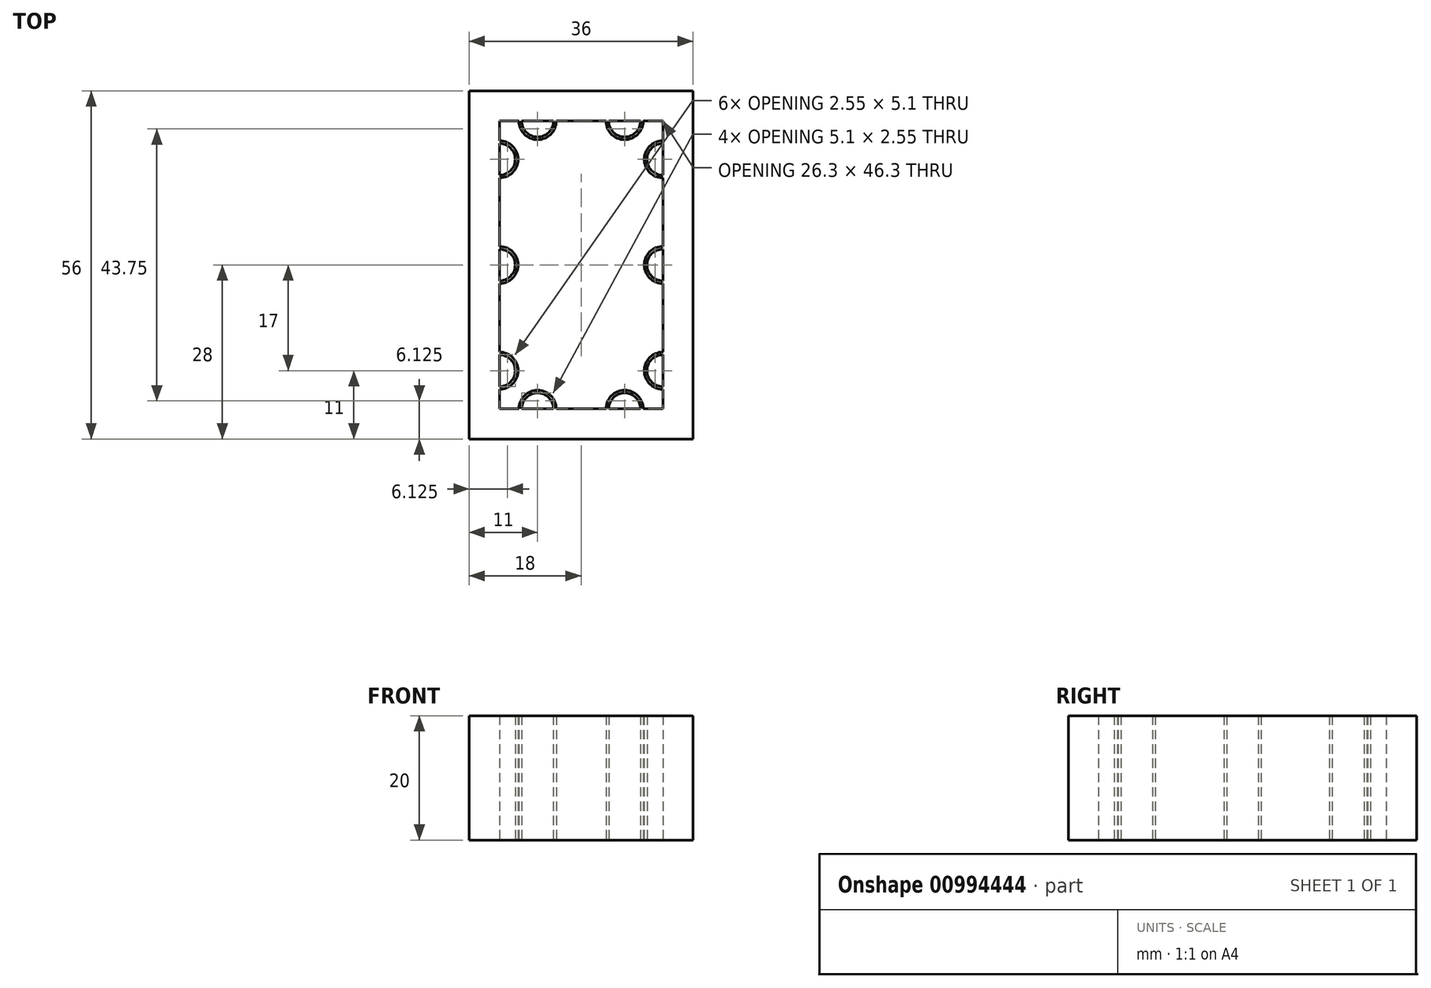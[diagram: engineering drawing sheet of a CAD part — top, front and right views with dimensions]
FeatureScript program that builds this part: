
annotation { "Feature Type Name" : "Feature", "Feature Type Description" : "" }
export const myFeature = defineFeature(function(context is Context, id is Id, definition is map)
    precondition{}
    {
        {
            var Q0;
            Q0=qCreatedBy(makeId("Top.planeOp"),FACE);
            var sketch = newSketch(context, id + "F0", { "sketchPlane" : qUnion([Q0])});
            skLineSegment(sketch, "E0.bottom", {"start": v(0, 0) * mm, "end": v(20, 0) * mm, "construction": true});
            skLineSegment(sketch, "E0.top", {"start": v(0, 40) * mm, "end": v(20, 40) * mm, "construction": true});
            skLineSegment(sketch, "E0.left", {"start": v(0, 0) * mm, "end": v(0, 40) * mm, "construction": true});
            skLineSegment(sketch, "E0.right", {"start": v(20, 0) * mm, "end": v(20, 40) * mm, "construction": true});
            skLineSegment(sketch, "E1", {"start": v(6, 40) * mm, "end": v(6, 34) * mm, "construction": true});
            skLineSegment(sketch, "E2", {"start": v(14, 40) * mm, "end": v(14, 34) * mm, "construction": true});
            skLineSegment(sketch, "E3", {"start": v(1, 27) * mm, "end": v(1, 13) * mm, "construction": true});
            skLineSegment(sketch, "E4", {"start": v(19, 27) * mm, "end": v(19, 13) * mm, "construction": true});
            skLineSegment(sketch, "E5", {"start": v(14, 6) * mm, "end": v(14, 0) * mm, "construction": true});
            skLineSegment(sketch, "E6", {"start": v(6, 6) * mm, "end": v(6, 0) * mm, "construction": true});
            skPoint(sketch, "E7.centerSnap0", {"position": v(6, 37) * mm});
            skPoint(sketch, "E8.centerSnap0", {"position": v(14, 37) * mm});
            skPoint(sketch, "E9.centerSnap0", {"position": v(14, 3) * mm});
            skLineSegment(sketch, "E10.0", {"start": v(-3.15, 43.15) * mm, "end": v(0, 43.15) * mm});
            skLineSegment(sketch, "E10.1", {"start": v(-3.15, -3.15) * mm, "end": v(-3.15, 0) * mm});
            skLineSegment(sketch, "E10.2", {"start": v(-3.15, -3.15) * mm, "end": v(0, -3.15) * mm});
            skLineSegment(sketch, "E10.3", {"start": v(23.15, -3.15) * mm, "end": v(23.15, 0) * mm});
            skLineSegment(sketch, "E11.0", {"start": v(-8, 48) * mm, "end": v(28, 48) * mm});
            skLineSegment(sketch, "E11.1", {"start": v(-8, -8) * mm, "end": v(-8, 48) * mm});
            skLineSegment(sketch, "E11.2", {"start": v(-8, -8) * mm, "end": v(28, -8) * mm});
            skLineSegment(sketch, "E11.3", {"start": v(28, -8) * mm, "end": v(28, 48) * mm});
            skArc(sketch, "E12", {"start": v(-3.15, 34) * mm, "mid": v(-0.15, 37) * mm, "end": v(-3.15, 40) * mm});
            skArc(sketch, "E13", {"start": v(23.15, 40) * mm, "mid": v(20.15, 37) * mm, "end": v(23.15, 34) * mm});
            skArc(sketch, "E14", {"start": v(-3.15, 0) * mm, "mid": v(-0.15, 3) * mm, "end": v(-3.15, 6) * mm});
            skPoint(sketch, "E14.centerSnap0", {"position": v(6, 3) * mm});
            skArc(sketch, "E15", {"start": v(23.15, 6) * mm, "mid": v(20.15, 3) * mm, "end": v(23.15, 0) * mm});
            skArc(sketch, "E16", {"start": v(-3.15, 17) * mm, "mid": v(-0.15, 20) * mm, "end": v(-3.15, 23) * mm});
            skPoint(sketch, "E16.centerSnap0", {"position": v(1, 20) * mm});
            skArc(sketch, "E17", {"start": v(23.15, 23) * mm, "mid": v(20.15, 20) * mm, "end": v(23.15, 17) * mm});
            skPoint(sketch, "E17.centerSnap0", {"position": v(23.15, 20) * mm});
            skPoint(sketch, "E17.centerSnap1", {"position": v(19, 20) * mm});
            skArc(sketch, "E18", {"start": v(14, 43.15) * mm, "mid": v(17, 40.15) * mm, "end": v(20, 43.15) * mm});
            skArc(sketch, "E19", {"start": v(0, 43.15) * mm, "mid": v(3, 40.15) * mm, "end": v(6, 43.15) * mm});
            skArc(sketch, "E20", {"start": v(0.45, 43.15) * mm, "mid": v(3, 40.6) * mm, "end": v(5.55, 43.15) * mm});
            skArc(sketch, "E21", {"start": v(14.45, 43.15) * mm, "mid": v(17, 40.6) * mm, "end": v(19.55, 43.15) * mm});
            skArc(sketch, "E22", {"start": v(-3.15, 34.45) * mm, "mid": v(-0.6, 37) * mm, "end": v(-3.15, 39.55) * mm});
            skArc(sketch, "E23", {"start": v(-3.15, 17.45) * mm, "mid": v(-0.6, 20) * mm, "end": v(-3.15, 22.55) * mm});
            skArc(sketch, "E24", {"start": v(-3.15, 0.45) * mm, "mid": v(-0.6, 3) * mm, "end": v(-3.15, 5.55) * mm});
            skArc(sketch, "E25", {"start": v(23.15, 5.55) * mm, "mid": v(20.6, 3) * mm, "end": v(23.15, 0.45) * mm});
            skArc(sketch, "E26", {"start": v(23.15, 22.55) * mm, "mid": v(20.6, 20) * mm, "end": v(23.15, 17.45) * mm});
            skArc(sketch, "E27", {"start": v(23.15, 39.55) * mm, "mid": v(20.6, 37) * mm, "end": v(23.15, 34.45) * mm});
            skLineSegment(sketch, "E28.trimOffspring", {"start": v(-3.15, 40) * mm, "end": v(-3.15, 43.15) * mm});
            skLineSegment(sketch, "E29.trimOffspring", {"start": v(-3.15, 34.45) * mm, "end": v(-3.15, 39.55) * mm});
            skLineSegment(sketch, "E30.trimOffspring", {"start": v(-3.15, 23) * mm, "end": v(-3.15, 34) * mm});
            skLineSegment(sketch, "E31.trimOffspring", {"start": v(-3.15, 17.45) * mm, "end": v(-3.15, 22.55) * mm});
            skLineSegment(sketch, "E32.trimOffspring", {"start": v(-3.15, 0.45) * mm, "end": v(-3.15, 5.55) * mm});
            skLineSegment(sketch, "E33.trimOffspring", {"start": v(-3.15, 6) * mm, "end": v(-3.15, 17) * mm});
            skLineSegment(sketch, "E34.trimOffspring", {"start": v(23.15, 0.45) * mm, "end": v(23.15, 5.55) * mm});
            skLineSegment(sketch, "E35.trimOffspring", {"start": v(23.15, 6) * mm, "end": v(23.15, 17) * mm});
            skLineSegment(sketch, "E36.trimOffspring", {"start": v(23.15, 17.45) * mm, "end": v(23.15, 22.55) * mm});
            skLineSegment(sketch, "E37.trimOffspring", {"start": v(23.15, 23) * mm, "end": v(23.15, 34) * mm});
            skLineSegment(sketch, "E38.trimOffspring", {"start": v(23.15, 34.45) * mm, "end": v(23.15, 39.55) * mm});
            skLineSegment(sketch, "E39.trimOffspring", {"start": v(23.15, 40) * mm, "end": v(23.15, 43.15) * mm});
            skLineSegment(sketch, "E40.trimOffspring", {"start": v(20, 43.15) * mm, "end": v(23.15, 43.15) * mm});
            skLineSegment(sketch, "E41.trimOffspring", {"start": v(14.45, 43.15) * mm, "end": v(19.55, 43.15) * mm});
            skLineSegment(sketch, "E42.trimOffspring", {"start": v(6, 43.15) * mm, "end": v(14, 43.15) * mm});
            skLineSegment(sketch, "E43.trimOffspring", {"start": v(0.45, 43.15) * mm, "end": v(5.55, 43.15) * mm});
            skArc(sketch, "E44", {"start": v(6, -3.15) * mm, "mid": v(3, -0.15) * mm, "end": v(0, -3.15) * mm});
            skArc(sketch, "E45", {"start": v(5.55, -3.15) * mm, "mid": v(3, -0.6) * mm, "end": v(0.45, -3.15) * mm});
            skArc(sketch, "E46", {"start": v(20, -3.15) * mm, "mid": v(17, -0.15) * mm, "end": v(14, -3.15) * mm});
            skArc(sketch, "E47", {"start": v(19.55, -3.15) * mm, "mid": v(17, -0.6) * mm, "end": v(14.45, -3.15) * mm});
            skLineSegment(sketch, "E48.trimOffspring", {"start": v(0.45, -3.15) * mm, "end": v(5.55, -3.15) * mm});
            skLineSegment(sketch, "E49.trimOffspring", {"start": v(6, -3.15) * mm, "end": v(14, -3.15) * mm});
            skLineSegment(sketch, "E50.trimOffspring", {"start": v(14.45, -3.15) * mm, "end": v(19.55, -3.15) * mm});
            skLineSegment(sketch, "E51.trimOffspring", {"start": v(20, -3.15) * mm, "end": v(23.15, -3.15) * mm});
            skSolve(sketch);
        }
        {
            var Q0;
            Q0 = qSketchRegion(id + "F0", true);
            extrude(context, id + "F1", {"entities" : qUnion([Q0]), "depth" : 20 * mm, "offsetDistance" : 25 * mm});
        }
    });
